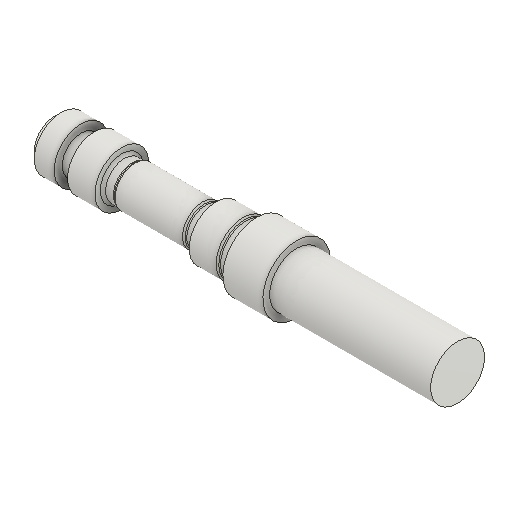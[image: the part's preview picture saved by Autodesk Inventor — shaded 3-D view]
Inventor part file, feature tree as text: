
AUTODESK INVENTOR PART (.ipt)
format: ipt  version: 2025.1 (Build 291241000, 241)  size: 190,976 bytes
history: native  units: mm
features: other x13, revolve x1, chamfer x1
ambient origin geometry x6: Origin, XZ Plane, XY Plane, X Axis, Y Axis, Z Axis
bodies: Body1 (feature_tree)
feature tree (15):
  other  "{BB8FE430-83BF-418D-8DF9-9B323D3DB9B9}"
  other  "Bryła1"
  revolve  "Obrót1"
  other  "Podcięcie3"
  other  "Podcięcie4"
  other  "Podcięcie2"
  chamfer  "Faza1"  [1 undecoded]
  other  "Rowek dla pierścienia zabezpieczającego1"
  other  "Płaszczyzna początkowa"
  other  "Punkt początkowy"
  other  "Szkic główny"
  other  "iFeature27:1"
  other  "iFeature2:1"
  other  "iFeature2:2"
  other  "iFeature2:3"
note: 1 required parameter value undecoded (feature->parameter linkage not recoverable at this tier; creation-order binding heuristic only, values carry confidence <= 0.55)
